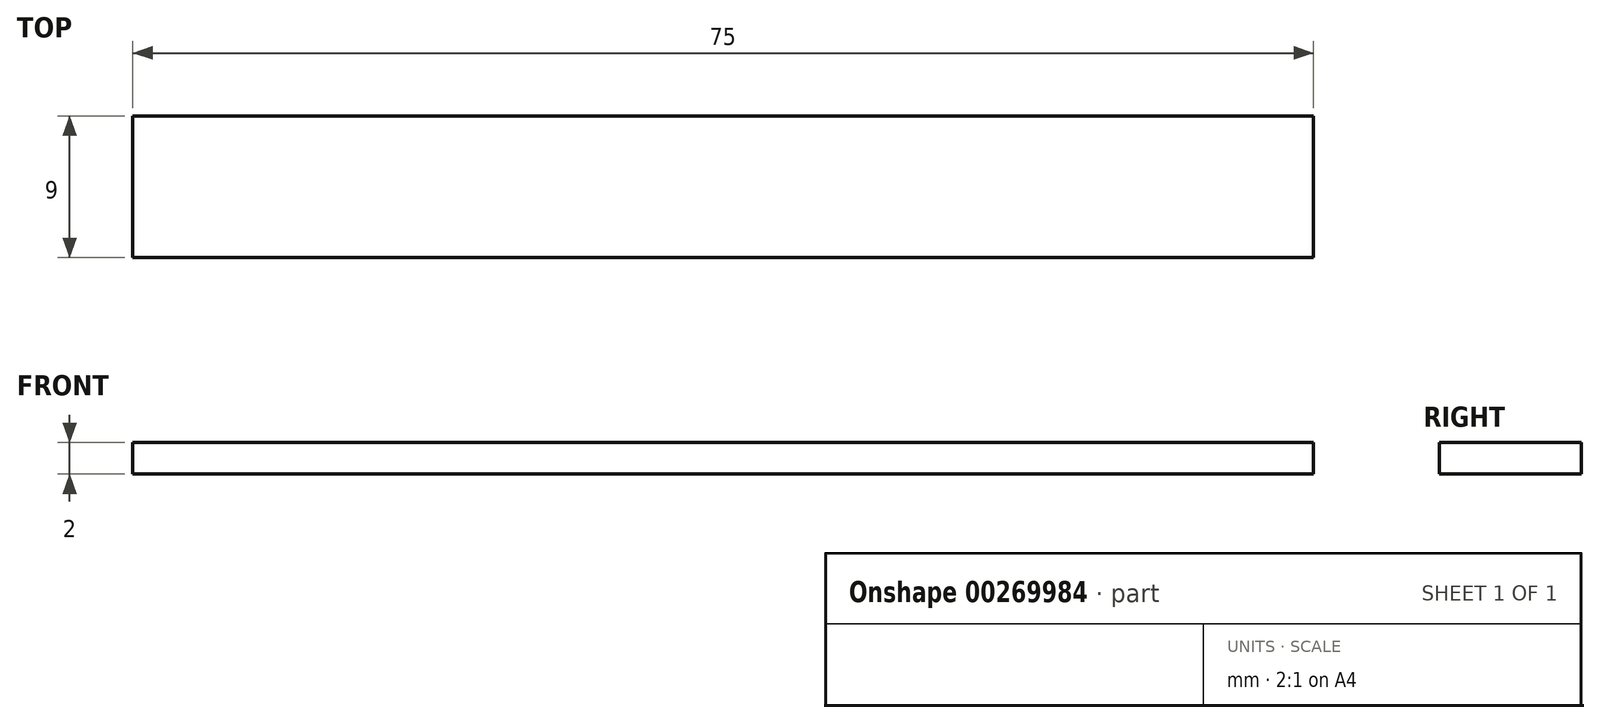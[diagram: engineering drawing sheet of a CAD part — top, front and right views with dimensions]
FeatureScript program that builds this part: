
annotation { "Feature Type Name" : "Feature", "Feature Type Description" : "" }
export const myFeature = defineFeature(function(context is Context, id is Id, definition is map)
    precondition{}
    {
        {
            var Q0;
            Q0=qCreatedBy(makeId("Top.planeOp"),FACE);
            var sketch = newSketch(context, id + "F0", { "sketchPlane" : qUnion([Q0])});
            skLineSegment(sketch, "E0.bottom", {"start": v(37.5, 3) * mm, "end": v(-37.5, 3) * mm});
            skLineSegment(sketch, "E0.top", {"start": v(37.5, -3) * mm, "end": v(-37.5, -3) * mm});
            skLineSegment(sketch, "E0.left", {"start": v(37.5, 3) * mm, "end": v(37.5, -3) * mm});
            skLineSegment(sketch, "E0.right", {"start": v(-37.5, 3) * mm, "end": v(-37.5, -3) * mm});
            skPoint(sketch, "E0.middle", {"position": v(0, 0) * mm});
            skSolve(sketch);
        }
        {
            var Q0;
            Q0=qCreatedBy(makeId("Top.planeOp"),FACE);
            cPlane(context, id + "F1", {"entities" : qUnion([Q0]), "cplaneType" : CPlaneType.OFFSET, "offset" : 2 * mm, "width" : 150 * mm, "height" : 150 * mm});
        }
        {
            var Q0;
            Q0=qCreatedBy(id+"F1.planeOp",FACE);
            var sketch = newSketch(context, id + "F2", { "sketchPlane" : qUnion([Q0])});
            skLineSegment(sketch, "E1", {"start": v(-35.5, 0) * mm, "end": v(35.5, 0) * mm});
            skSolve(sketch);
        }
        {
            var Q0;
            Q0=sQuery(id+"F0.wireOp",EDGE,"E0.right");
            var Q1;
            Q1=sQuery(id+"F2.wireOp",VERTEX,"E1.start");
            loft(context, id + "F3", {"bodyType" : ToolBodyType.SURFACE, "wireProfilesArray" : [{ "wireProfileEntities" : qUnion([Q0]) }, { "wireProfileEntities" : qUnion([Q1]) }]});
        }
        {
            var Q0;
            Q0=sQuery(id+"F0.wireOp",EDGE,"E0.bottom");
            var Q1;
            Q1=sQuery(id+"F2.wireOp",EDGE,"E1");
            loft(context, id + "F4", {"bodyType" : ToolBodyType.SURFACE, "wireProfilesArray" : [{ "wireProfileEntities" : qUnion([Q0]) }, { "wireProfileEntities" : qUnion([Q1]) }]});
        }
        {
            var Q0;
            Q0=sQuery(id+"F0.wireOp",EDGE,"E0.top");
            var Q1;
            Q1=sQuery(id+"F2.wireOp",EDGE,"E1");
            loft(context, id + "F5", {"bodyType" : ToolBodyType.SURFACE, "wireProfilesArray" : [{ "wireProfileEntities" : qUnion([Q0]) }, { "wireProfileEntities" : qUnion([Q1]) }]});
        }
        {
            var Q0;
            Q0=sQuery(id+"F0.wireOp",EDGE,"E0.left");
            var Q1;
            Q1=sQuery(id+"F2.wireOp",VERTEX,"E1.end");
            loft(context, id + "F6", {"bodyType" : ToolBodyType.SURFACE, "wireProfilesArray" : [{ "wireProfileEntities" : qUnion([Q0]) }, { "wireProfileEntities" : qUnion([Q1]) }]});
        }
        {
            var Q0;
            Q0=qCreatedBy(makeId("Top.planeOp"),FACE);
            var sketch = newSketch(context, id + "F7", { "sketchPlane" : qUnion([Q0])});
            skLineSegment(sketch, "E2.bottom", {"start": v(-37.5, -3) * mm, "end": v(37.5, -3) * mm});
            skLineSegment(sketch, "E2.top", {"start": v(-37.5, 6) * mm, "end": v(37.5, 6) * mm});
            skLineSegment(sketch, "E2.left", {"start": v(-37.5, -3) * mm, "end": v(-37.5, 6) * mm});
            skLineSegment(sketch, "E2.right", {"start": v(37.5, -3) * mm, "end": v(37.5, 6) * mm});
            skSolve(sketch);
        }
        {
            var Q0;
            Q0=makeQuery(id+"F7.imprint","IMPRINT",FACE,{"disambiguationData":[TD([[makeQuery(id+"F7.imprint","IMPRINT",EDGE,{"derivedFrom":sQuery(id+"F7.wireOp",EDGE,"E2.bottom")}),1.0]])]});
            extrude(context, id + "F8", {"entities" : qUnion([Q0]), "oppositeDirection" : true, "depth" : 2 * mm});
        }
    });
